# Revit family: IS_Sphero_E1832_BIM_GB
name_source: partatom
category: Plumbing Fixtures
revit_build: Autodesk Revit 2017 (Build: 20160225_1515(x64)
units: mm (PartAtom-declared; Revit-internal decimal feet)

## family parameters
Always vertical = No
Cut with Voids When Loaded = No
OmniClass Number = 23.45.05.21.11.21
OmniClass Title = Urinals
Part Type = Normal
Room Calculation Point = No
Round Connector Dimension = Use Diameter
Shared = No
Work Plane-Based = No

## types (1)
- E183201 - Sphero MAXI BI Closed Shroud Urinal
    Accessories = https://www.idealstandard.be
    AreaUnits = millimeters
    AssetType = Fixed
    BIMObjectName = IS_IdealStandard_WallHungUrinals_Sphero_E1832
    BIMobject category = Urinals
    BIMobject category code = sanitary-urinals
    BIMobject main category = Sanitary
    BIMobject main category code = sanitary
    BarCode = 5017830543121
    Brand = Ideal Standard
    Brand url = https://www.idealstandard.be
    CisternCapacity = 0.00 m³
    Color = White
    ConnectionType = PLUMBING
    CurrencyUnit = £
    CurrentRevision = 1
    Description = Sphero Maxi Back Inlet rimless urinal concealed trap, , easy fix hanger, top fixed waste & back inlet water connection pack with service valve, spreader & flow regulator included
    DrainSize = 0 mm  [stored 0 ft]
    DurationUnit = Years
    Edition number = 1
    ExpectedLife = 30
    Features = Maxi Back Inlet rimless urinal concealed trap, , easy fix hanger, top fixed waste & back inlet water connection pack with service valve, spreader & flow regulator included
    Finish = White
    FlushRate = 0.00 m³
    FlushingRate = 0
    GTIN code = https://5017830543121
    HasGrabHandles = No
    HasIntegralShutOffDevice = No
    HasTray = No
    Help = https://www.idealstandard.be
    IFC Classification = Sanitary Terminal
    IfcExportAs = IfcSanitaryTerminalType
    IfcExportType = URINAL
    InletConnectionSize = 0 mm  [stored 0 ft]
    Installation instructions = https://www.idealstandard.be
    InstallationInstructions = https://www.idealstandard.be
    IsAutomaticFlush = No
    IsBuiltIn = No
    IsHighPressure = No
    IsSingleFlush = No
    LinearUnits = millimeters
    MainColor = White
    MaintenanceInformation = https://www.idealstandard.be
    Manufacturer = Ideal Standard
    Manufacturer name = Ideal Standard
    ManufacturerURL = https://www.idealstandard.be
    Material = Ceramics
    Material main = Ceramics
    MaterialThickness = 0 mm  [stored 0 ft]
    Model = E183201
    ModelNumber = E1832
    ModelReference = E183201
    NBS Reference Code = 35-93-82
    NBS Reference Description = Wall-Hung Urinals
    Name = WallHungUrinals_Sphero_E1832_IdealStandard
    NettWeight = 18.9
    NominalDepth = 300 mm
    NominalHeight = 620 mm
    NominalLength = 300 mm
    NominalWidth = 299 mm
    OmniClass Code = 23-31 21 00
    OmniClass Description = Urinals
    OutletConnectionSize = 0 mm  [stored 0 ft]
    Product Guid = 7c97f927-01ef-4baf-b205-4af6eee52bf9
    Product SKU = E1832
    Product data url = https://bimobject.com
    Product family = Sphero
    Product group = Urinals
    Product name = Sphero MAXI BI Urinal
    Product url = https://www.idealstandard.be
    ProductInformation = https://www.idealstandard.be
    QR code = http://bimobject.com
    SeatHasCover = No
    Shape = Sculptured
    Size = 300 x 300 x 620 mm
    Space = Internal
    SpilloverLevel = 0 mm  [stored 0 ft]
    Technical description = https://www.idealstandard.be
    UNSPSC Code = 301815
    URL = https://www.idealstandard.be
    Uniclass 1.4 Code = L7217
    Uniclass 1.4 Description = Urinals
    Uniclass 2.0 Code = PR-35-93-82
    Uniclass 2.0 Description = Wall-Hung Urinals
    Uniclass 2015 Code = Pr_40_20_93_82
    Uniclass 2015 Name = Wall-hung urinals
    Uniclass2015Code = Pr_40_20_93_82
    Uniclass2015Title = Wall-hung urinals
    Uniclass2015Version = v1.1
    UrinalColor = White
    UrinalMaterial = Ceramics
    UrinalType = Wall hung
    Version = 1
    VolumeUnits = Litres
    WRASURL = https://www.wras.co.uk
    WarrantyDescription = Manufacturers warranty
    WarrantyDurationParts = 99
    WarrantyDurationUnit = Years
    WarrantyGuarantorParts = https://www.idealstandard.be

note: [stored X ft] marks values corroborated as IEEE doubles in the binary element streams (Revit-internal decimal feet)

## geometry (parser evidence)
native form markers: Sweep x1
no freeform markers — native parametric forms only
